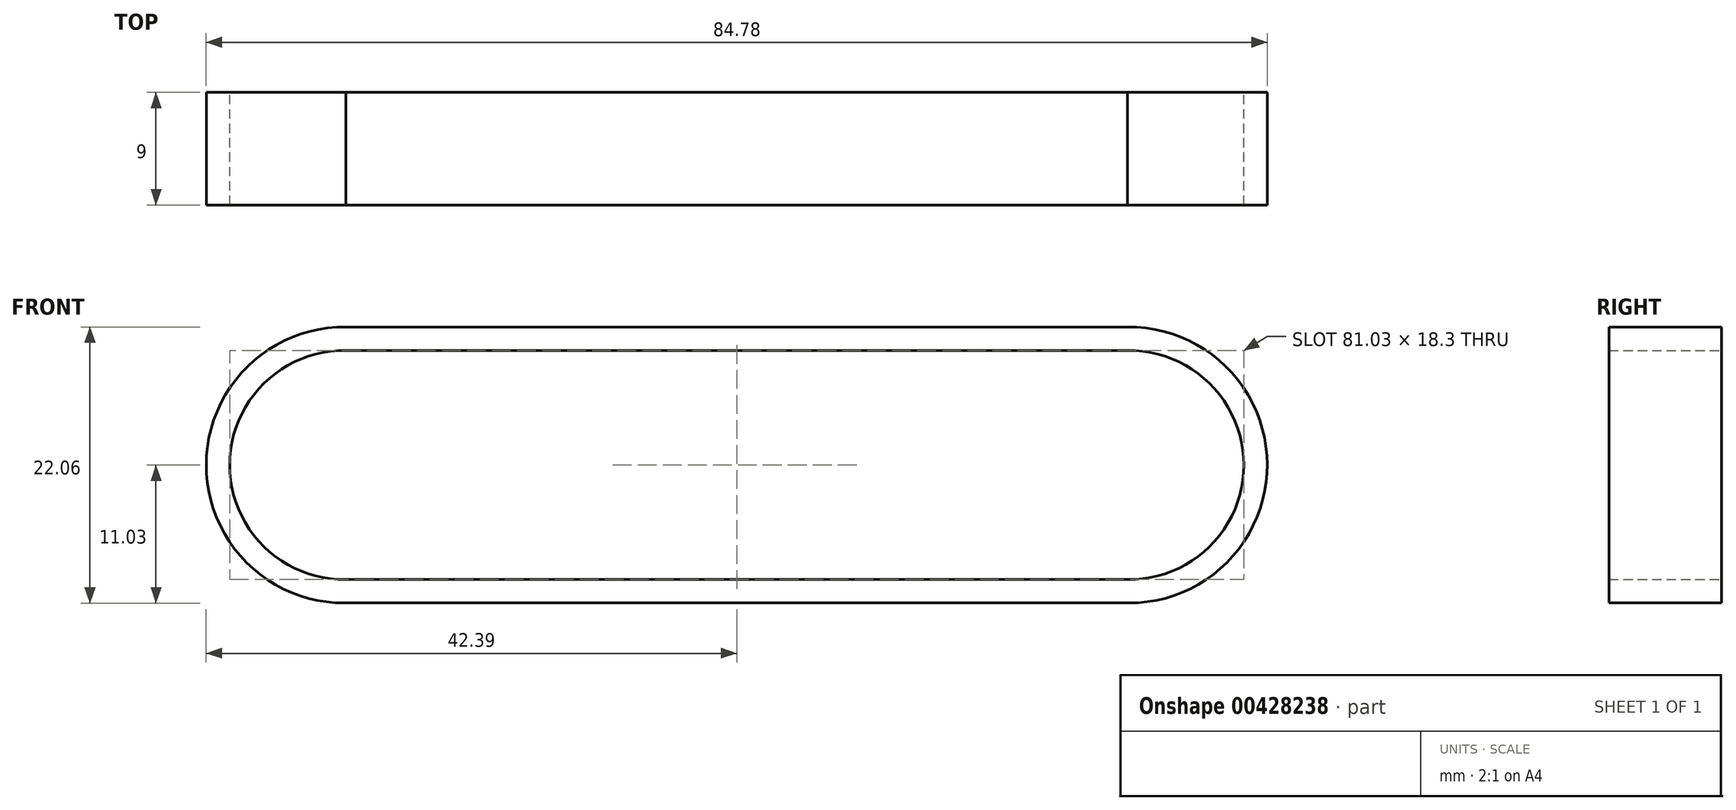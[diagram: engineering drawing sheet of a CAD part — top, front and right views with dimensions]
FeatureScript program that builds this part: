
annotation { "Feature Type Name" : "Feature", "Feature Type Description" : "" }
export const myFeature = defineFeature(function(context is Context, id is Id, definition is map)
    precondition{}
    {
        {
            var Q0;
            Q0=qCreatedBy(makeId("Front.planeOp"),FACE);
            var sketch = newSketch(context, id + "F0", { "sketchPlane" : qUnion([Q0])});
            skLineSegment(sketch, "E0", {"start": v(31.23, 9.15) * mm, "end": v(31.23, 9.15) * mm});
            skLineSegment(sketch, "E1", {"start": v(31.24, -9.15) * mm, "end": v(0, -9.15) * mm});
            skLineSegment(sketch, "E2", {"start": v(31.21, 11.02) * mm, "end": v(0, 11.02) * mm});
            skLineSegment(sketch, "E3", {"start": v(31.33, -11.03) * mm, "end": v(0, -11.03) * mm});
            skLineSegment(sketch, "E4", {"start": v(31.23, 9.15) * mm, "end": v(0, 9.15) * mm});
            skArc(sketch, "E5", {"start": v(31.2, 11.02) * mm, "mid": v(20.34, -0.07) * mm, "end": v(31.33, -11.03) * mm, "construction": true});
            skArc(sketch, "E6", {"start": v(31.33, -11.03) * mm, "mid": v(42.39, 0.07) * mm, "end": v(31.2, 11.02) * mm});
            skArc(sketch, "E7", {"start": v(31.24, -9.15) * mm, "mid": v(40.51, 0) * mm, "end": v(31.23, 9.15) * mm});
            skArc(sketch, "E8", {"start": v(31.23, 9.15) * mm, "mid": v(22.21, 0) * mm, "end": v(31.24, -9.15) * mm, "construction": true});
            skLineSegment(sketch, "E9.MirrorCS", {"start": v(-31.21, 11.02) * mm, "end": v(0, 11.02) * mm});
            skLineSegment(sketch, "E10.MirrorCS", {"start": v(-31.23, 9.15) * mm, "end": v(0, 9.15) * mm});
            skArc(sketch, "E11.MirrorCS", {"start": v(-31.24, -9.15) * mm, "mid": v(-40.51, 0) * mm, "end": v(-31.23, 9.15) * mm});
            skArc(sketch, "E12.MirrorCS", {"start": v(-31.33, -11.03) * mm, "mid": v(-42.39, 0.07) * mm, "end": v(-31.2, 11.02) * mm});
            skLineSegment(sketch, "E13.MirrorCS", {"start": v(-31.24, -9.15) * mm, "end": v(0, -9.15) * mm});
            skLineSegment(sketch, "E14.MirrorCS", {"start": v(-31.33, -11.03) * mm, "end": v(0, -11.03) * mm});
            skSolve(sketch);
        }
        {
            var Q0;
            Q0=makeQuery(id+"F0.imprint","IMPRINT",FACE,{"disambiguationData":[TD([[makeQuery(id+"F0.imprint","IMPRINT",EDGE,{"derivedFrom":sQuery(id+"F0.wireOp",EDGE,"E1")}),1.0]])]});
            extrude(context, id + "F1", {"entities" : qUnion([Q0]), "depth" : 9 * mm, "offsetDistance" : 25.4 * mm});
        }
    });
